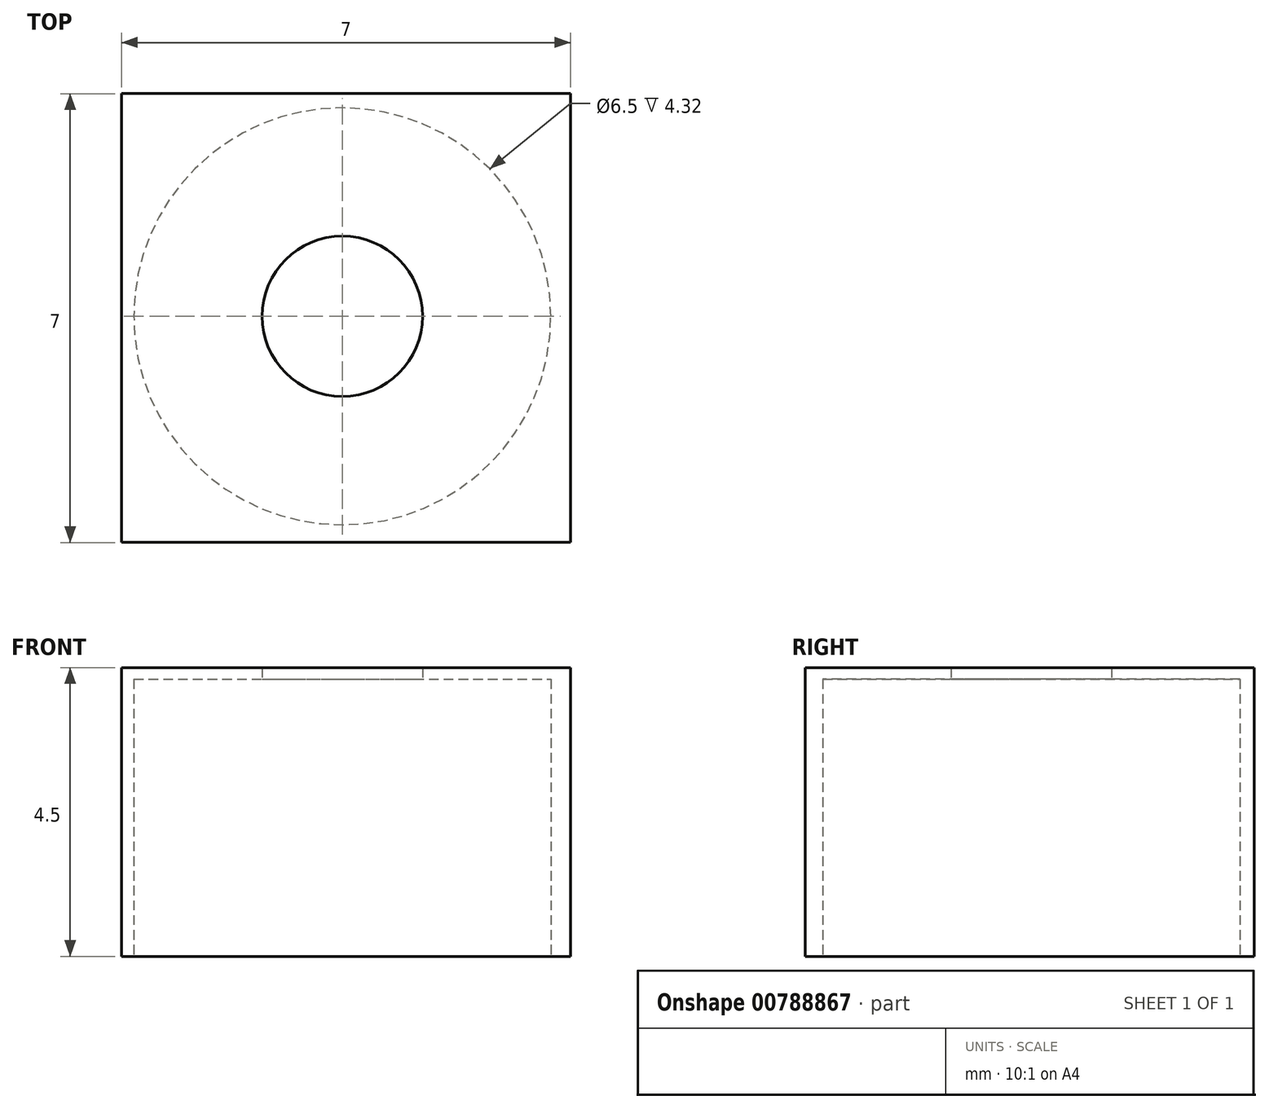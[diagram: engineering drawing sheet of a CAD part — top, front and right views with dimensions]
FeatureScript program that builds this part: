
annotation { "Feature Type Name" : "Feature", "Feature Type Description" : "" }
export const myFeature = defineFeature(function(context is Context, id is Id, definition is map)
    precondition{}
    {
        {
            var Q0;
            Q0=qCreatedBy(makeId("Top.planeOp"),FACE);
            var sketch = newSketch(context, id + "F0", { "sketchPlane" : qUnion([Q0])});
            skLineSegment(sketch, "E0", {"start": v(-17.37, 1.37) * mm, "end": v(-17.37, -5.63) * mm});
            skLineSegment(sketch, "E1", {"start": v(-17.37, 1.37) * mm, "end": v(-10.37, 1.37) * mm});
            skLineSegment(sketch, "E2", {"start": v(-10.37, 1.37) * mm, "end": v(-10.37, -5.63) * mm});
            skLineSegment(sketch, "E3", {"start": v(-10.37, -5.63) * mm, "end": v(-17.37, -5.63) * mm});
            skSolve(sketch);
        }
        {
            var Q0;
            Q0=makeQuery(id+"F0.imprint","IMPRINT",FACE,{"disambiguationData":[TD([[makeQuery(id+"F0.imprint","IMPRINT",EDGE,{"derivedFrom":sQuery(id+"F0.wireOp",EDGE,"E0")}),1.0]])]});
            extrude(context, id + "F1", {"entities" : qUnion([Q0]), "depth" : 4.5 * mm, "offsetDistance" : 25 * mm});
        }
        {
            var Q0;
            Q0=makeQuery(id+"F1.opExtrude","CAP_FACE",FACE,{"disambiguationData":[OSD([sQuery(id+"F0.wireOp",EDGE,"E0"),sQuery(id+"F0.wireOp",EDGE,"E1"),sQuery(id+"F0.wireOp",EDGE,"E2"),sQuery(id+"F0.wireOp",EDGE,"E3")])],"isStart":true});
            var sketch = newSketch(context, id + "F2", { "sketchPlane" : qUnion([Q0])});
            skCircle(sketch, "E4", {"center": v(-13.95, 2.13) * mm, "radius": 3.5 * mm});
            skPoint(sketch, "E4.first.point", {"position": v(-14.03, -1.37) * mm});
            skPoint(sketch, "E4.second.point", {"position": v(-14.03, 5.63) * mm});
            skPoint(sketch, "E4.third.point", {"position": v(-13.87, 5.63) * mm});
            skSolve(sketch);
        }
        {
            var Q0;
            {var subQ0=sQuery(id+"F2.wireOp",EDGE,"E4");var subQ4=makeQuery(id+"F1.opExtrude","CAP_EDGE",EDGE,{"disambiguationData":[OSD([sQuery(id+"F0.wireOp",EDGE,"E3")])],"isStart":true});var subQ9=makeQuery(id+"F2.imprint","INTERSECT",VERTEX,{"disambiguationData":[OD(0.0)],"derivedFrom":[subQ4,subQ0]});Q0=makeQuery(id+"F2.imprint","IMPRINT",FACE,{"disambiguationData":[TD([[makeQuery(id+"F2.imprint","IMPRINT",EDGE,{"disambiguationData":[TD([[subQ9,-1.0]])],"derivedFrom":subQ0}),1.0]])]});}
            var sketch = newSketch(context, id + "F3", { "sketchPlane" : qUnion([Q0])});
            skCircle(sketch, "E5", {"center": v(-13.93, 2.1) * mm, "radius": 3.25 * mm});
            skCircle(sketch, "E6", {"center": v(-13.93, 2.1) * mm, "radius": 1.25 * mm});
            skSolve(sketch);
        }
        {
            var Q0;
            Q0=makeQuery(id+"F3.imprint","IMPRINT",FACE,{"disambiguationData":[TD([[makeQuery(id+"F3.imprint","IMPRINT",EDGE,{"derivedFrom":sQuery(id+"F3.wireOp",EDGE,"E6")}),1.0]])]});
            extrude(context, id + "F4", {"entities" : qUnion([Q0]), "operationType" : NewBodyOperationType.REMOVE, "oppositeDirection" : true, "depth" : 25 * mm, "offsetDistance" : 25 * mm});
        }
        {
            var Q0;
            Q0 = qSketchRegion(id + "F3", true);
            extrude(context, id + "F5", {"entities" : qUnion([Q0]), "operationType" : NewBodyOperationType.REMOVE, "oppositeDirection" : true, "depth" : 4.32 * mm, "offsetDistance" : 25 * mm});
        }
    });
